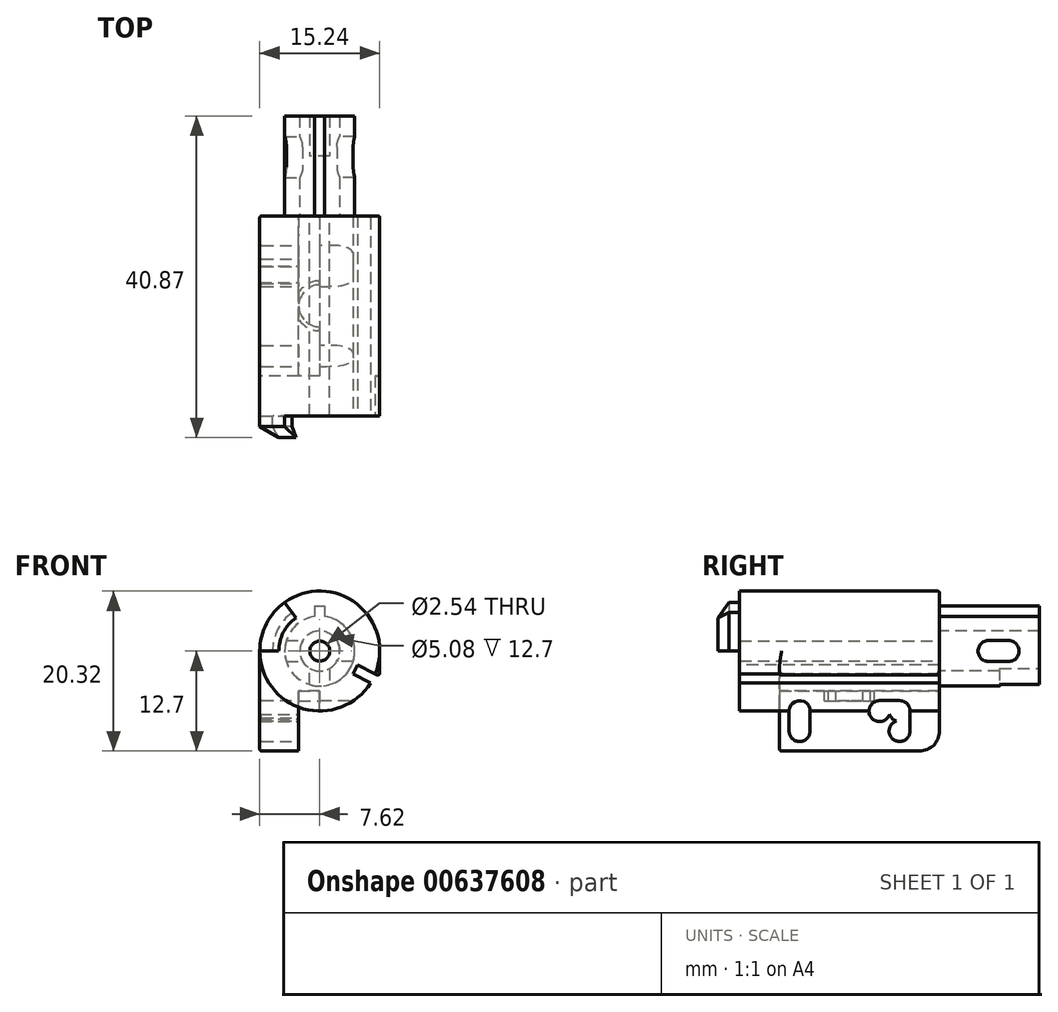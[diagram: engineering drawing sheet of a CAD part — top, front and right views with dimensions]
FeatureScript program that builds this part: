
annotation { "Feature Type Name" : "Feature", "Feature Type Description" : "" }
export const myFeature = defineFeature(function(context is Context, id is Id, definition is map)
    precondition{}
    {
        {
            var Q0;
            Q0=qCreatedBy(makeId("Front.planeOp"),FACE);
            var sketch = newSketch(context, id + "F0", { "sketchPlane" : qUnion([Q0])});
            skPoint(sketch, "E0.middle", {"position": v(0, 0) * mm});
            skLineSegment(sketch, "E1.bottom", {"start": v(7.62, 37.7) * mm, "end": v(-7.62, 37.7) * mm});
            skLineSegment(sketch, "E1.top", {"start": v(7.62, -37.7) * mm, "end": v(-7.62, -37.7) * mm});
            skLineSegment(sketch, "E1.left", {"start": v(7.62, 37.7) * mm, "end": v(7.62, -37.7) * mm});
            skLineSegment(sketch, "E1.right", {"start": v(-7.62, 37.7) * mm, "end": v(-7.62, -37.7) * mm});
            skCircle(sketch, "E2", {"center": v(0, 0) * mm, "radius": 7.62 * mm});
            skCircle(sketch, "E3", {"center": v(0, 0) * mm, "radius": 1.27 * mm});
            skSolve(sketch);
        }
        {
            var Q0;
            Q0=makeQuery(id+"F0.imprint","IMPRINT",FACE,{"disambiguationData":[TD([[makeQuery(id+"F0.imprint","IMPRINT",EDGE,{"derivedFrom":sQuery(id+"F0.wireOp",EDGE,"E3")}),-1.0]])]});
            extrude(context, id + "F1", {"entities" : qUnion([Q0]), "depth" : 12.7 * mm});
        }
        {
            var Q0;
            Q0=makeQuery(id+"F1.opExtrude","CAP_FACE",FACE,{"disambiguationData":[OSD([sQuery(id+"F0.wireOp",EDGE,"E2"),sQuery(id+"F0.wireOp",EDGE,"E3")])],"isStart":false});
            var sketch = newSketch(context, id + "F2", { "sketchPlane" : qUnion([Q0])});
            skArc(sketch, "E4", {"start": v(-7.62, 0) * mm, "mid": v(-6.78, 3.48) * mm, "end": v(-4.44, 6.2) * mm});
            skArc(sketch, "E5.0", {"start": v(-6, 0) * mm, "mid": v(-5.34, 2.74) * mm, "end": v(-3.5, 4.88) * mm});
            skLineSegment(sketch, "E6", {"start": v(-4.44, 6.2) * mm, "end": v(-3.5, 4.88) * mm});
            skLineSegment(sketch, "E7", {"start": v(-7.62, 0) * mm, "end": v(-6, 0) * mm});
            skSolve(sketch);
        }
        {
            var Q0;
            Q0=qSketchRegion(id+"F2",true);
            extrude(context, id + "F3", {"entities" : qUnion([Q0]), "operationType" : NewBodyOperationType.ADD, "depth" : 1.37 * mm});
        }
        {
            var Q0;
            Q0=makeQuery(id+"F3.opExtrude","CAP_FACE",FACE,{"disambiguationData":[OSD([sQuery(id+"F2.wireOp",EDGE,"E4"),sQuery(id+"F2.wireOp",EDGE,"E5.0"),sQuery(id+"F2.wireOp",EDGE,"E6"),sQuery(id+"F2.wireOp",EDGE,"E7")])],"isStart":false});
            cPlane(context, id + "F4", {"entities" : qUnion([Q0]), "cplaneType" : CPlaneType.OFFSET, "offset" : 1.4 * mm, "width" : 152.4 * mm, "height" : 152.4 * mm});
        }
        {
            var Q0;
            Q0=qCreatedBy(id+"F4.planeOp",FACE);
            var sketch = newSketch(context, id + "F5", { "sketchPlane" : qUnion([Q0])});
            skArc(sketch, "E8.0", {"start": v(-3.04, 4.23) * mm, "mid": v(-4.63, 2.38) * mm, "end": v(-5.2, 0) * mm});
            skSolve(sketch);
        }
        {
            var Q0;
            Q0=makeQuery(id+"F3.opExtrude","CAP_VERTEX",VERTEX,{"disambiguationData":[OSD([sQuery(id+"F0.wireOp",EDGE,"E2"),sQuery(id+"F2.wireOp",EDGE,"E4"),sQuery(id+"F2.wireOp",EDGE,"E7")])],"isStart":false});
            var Q1;
            Q1=makeQuery(id+"F3.opExtrude","CAP_VERTEX",VERTEX,{"disambiguationData":[OSD([sQuery(id+"F2.wireOp",EDGE,"E5.0"),sQuery(id+"F2.wireOp",EDGE,"E7")])],"isStart":false});
            var Q2;
            Q2=sQuery(id+"F5.wireOp",VERTEX,"E8.0.end");
            cPlane(context, id + "F6", {"entities" : qUnion([Q0, Q1, Q2]), "cplaneType" : CPlaneType.THREE_POINT, "offset" : 25.4 * mm, "width" : 152.4 * mm, "height" : 152.4 * mm});
        }
        {
            var Q0;
            Q0=qCreatedBy(id+"F6.planeOp",FACE);
            var sketch = newSketch(context, id + "F7", { "sketchPlane" : qUnion([Q0])});
            skPoint(sketch, "E9.0", {"position": v(-7.62, -14.07) * mm});
            skPoint(sketch, "E10.0", {"position": v(-6, -14.07) * mm});
            skPoint(sketch, "E11.0", {"position": v(-5.2, -15.47) * mm});
            skLineSegment(sketch, "E12", {"start": v(-7.62, -14.07) * mm, "end": v(-5.2, -15.47) * mm});
            skLineSegment(sketch, "E13", {"start": v(-5.2, -15.47) * mm, "end": v(-6, -14.07) * mm});
            skLineSegment(sketch, "E14", {"start": v(-6, -14.07) * mm, "end": v(-7.62, -14.07) * mm});
            skSolve(sketch);
        }
        {
            var Q0;
            Q0=makeQuery(id+"F3.opExtrude","CAP_VERTEX",VERTEX,{"disambiguationData":[OSD([sQuery(id+"F0.wireOp",EDGE,"E2"),sQuery(id+"F2.wireOp",EDGE,"E4"),sQuery(id+"F2.wireOp",EDGE,"E6")])],"isStart":false});
            var Q1;
            Q1=makeQuery(id+"F3.opExtrude","CAP_VERTEX",VERTEX,{"disambiguationData":[OSD([sQuery(id+"F2.wireOp",EDGE,"E5.0"),sQuery(id+"F2.wireOp",EDGE,"E6")])],"isStart":false});
            var Q2;
            Q2=sQuery(id+"F5.wireOp",VERTEX,"E8.0.start");
            cPlane(context, id + "F8", {"entities" : qUnion([Q0, Q1, Q2]), "cplaneType" : CPlaneType.THREE_POINT, "offset" : 25.4 * mm, "width" : 152.4 * mm, "height" : 152.4 * mm});
        }
        {
            var Q0;
            Q0=qCreatedBy(id+"F8.planeOp",FACE);
            var sketch = newSketch(context, id + "F9", { "sketchPlane" : qUnion([Q0])});
            skPoint(sketch, "E15.0", {"position": v(-14.07, 7.62) * mm});
            skPoint(sketch, "E16.0", {"position": v(-14.07, 6) * mm});
            skPoint(sketch, "E17.0", {"position": v(-15.47, 5.2) * mm});
            skLineSegment(sketch, "E18", {"start": v(-14.07, 7.62) * mm, "end": v(-14.07, 6) * mm});
            skLineSegment(sketch, "E19", {"start": v(-14.07, 6) * mm, "end": v(-15.47, 5.2) * mm});
            skLineSegment(sketch, "E20", {"start": v(-15.47, 5.2) * mm, "end": v(-14.07, 7.62) * mm});
            skSolve(sketch);
        }
        {
            var Q0;
            Q0=makeQuery(id+"F7.imprint","IMPRINT",FACE,{"disambiguationData":[TD([[makeQuery(id+"F7.imprint","IMPRINT",EDGE,{"derivedFrom":sQuery(id+"F7.wireOp",EDGE,"E12")}),1.0]])]});
            var Q1;
            Q1=makeQuery(id+"F9.imprint","IMPRINT",FACE,{"disambiguationData":[TD([[makeQuery(id+"F9.imprint","IMPRINT",EDGE,{"derivedFrom":sQuery(id+"F9.wireOp",EDGE,"E18")}),-1.0]])]});
            var Q2;
            Q2=makeQuery(id+"F7.imprint","IMPRINT",FACE,{"disambiguationData":[TD([[makeQuery(id+"F7.imprint","IMPRINT",EDGE,{"derivedFrom":sQuery(id+"F7.wireOp",EDGE,"E12")}),1.0]])]});
            var Q3;
            Q3=makeQuery(id+"F9.imprint","IMPRINT",FACE,{"disambiguationData":[TD([[makeQuery(id+"F9.imprint","IMPRINT",EDGE,{"derivedFrom":sQuery(id+"F9.wireOp",EDGE,"E18")}),-1.0]])]});
            var Q4;
            Q4=makeQuery(id+"F3.opExtrude","CAP_EDGE",EDGE,{"disambiguationData":[OSD([sQuery(id+"F2.wireOp",EDGE,"E4")])],"isStart":false});
            var Q5;
            Q5=makeQuery(id+"F3.opExtrude","CAP_EDGE",EDGE,{"disambiguationData":[OSD([sQuery(id+"F2.wireOp",EDGE,"E5.0")])],"isStart":false});
            var Q6;
            Q6=sQuery(id+"F5.wireOp",EDGE,"E8.0");
            loft(context, id + "F10", {"addGuides" : true, "sheetProfilesArray" : [{ "sheetProfileEntities" : qUnion([Q0]) }, { "sheetProfileEntities" : qUnion([Q1]) }], "wireProfilesArray" : [{ "wireProfileEntities" : qUnion([Q2]) }, { "wireProfileEntities" : qUnion([Q3]) }], "guidesArray" : [{ "guideEntities" : qUnion([Q4]), "guideDerivativeType" : LoftGuideDerivativeType.DEFAULT, "guideDerivativeMagnitude" : 1 }, { "guideEntities" : qUnion([Q5]), "guideDerivativeType" : LoftGuideDerivativeType.DEFAULT, "guideDerivativeMagnitude" : 1 }, { "guideEntities" : qUnion([Q6]), "guideDerivativeType" : LoftGuideDerivativeType.DEFAULT, "guideDerivativeMagnitude" : 1 }]});
        }
        {
            var Q0;
            Q0=makeQuery(id+"F1.opExtrude","CAP_FACE",FACE,{"disambiguationData":[OSD([sQuery(id+"F0.wireOp",EDGE,"E2"),sQuery(id+"F0.wireOp",EDGE,"E3")])],"isStart":true});
            var sketch = newSketch(context, id + "F11", { "sketchPlane" : qUnion([Q0])});
            skArc(sketch, "E21.0", {"start": v(-4.16, -6.39) * mm, "mid": v(-6.39, 4.16) * mm, "end": v(4.16, 6.39) * mm});
            skCircle(sketch, "E22", {"center": v(0, 0) * mm, "radius": 7.62 * mm});
            skSolve(sketch);
        }
        {
            var Q0;
            Q0=makeQuery(id+"F11.imprint","IMPRINT",FACE,{"disambiguationData":[TD([[makeQuery(id+"F11.imprint","IMPRINT",EDGE,{"derivedFrom":sQuery(id+"F11.wireOp",EDGE,"E22")}),1.0]])]});
            var Q1;
            Q1=makeQuery(id+"F11.imprint","IMPRINT",FACE,{"disambiguationData":[TD([[makeQuery(id+"F11.imprint","IMPRINT",EDGE,{"derivedFrom":makeQuery(id+"F1.opExtrude","CAP_EDGE",EDGE,{"disambiguationData":[OSD([sQuery(id+"F0.wireOp",EDGE,"E2")])],"isStart":true})}),-1.0]])]});
            var Q2;
            Q2=makeQuery(id+"F11.imprint","IMPRINT",FACE,{"disambiguationData":[TD([[makeQuery(id+"F11.imprint","IMPRINT",EDGE,{"derivedFrom":sQuery(id+"F11.wireOp",EDGE,"E22")}),-1.0]])]});
            extrude(context, id + "F12", {"entities" : qUnion([Q0, Q1, Q2]), "depth" : 12.7 * mm});
        }
        {
            var Q0;
            Q0=makeQuery(id+"FqKjOTA0KTiobea_0.opExtrude","SWEPT_BODY",BODY,{"disambiguationData":[OSD([sQuery(id+"F0.wireOp",EDGE,"uHF2WHmJ-zJ7i-FEed-3bSX-mTsy0IzEVw90"),sQuery(id+"F0.wireOp",EDGE,"k3DuiY5w-GI1o-rOdS-LLCr-VDr8IVeulzbr"),sQuery(id+"F0.wireOp",EDGE,"E1.left"),sQuery(id+"F0.wireOp",EDGE,"E1.right")])]});
            var Q1;
            Q1=makeQuery(id+"F1.opExtrude","SWEPT_BODY",BODY,{"disambiguationData":[OSD([sQuery(id+"F0.wireOp",EDGE,"E2"),sQuery(id+"F0.wireOp",EDGE,"E3")])]});
            var Q2;
            Q2=makeQuery(id+"F10.opLoft","SWEPT_BODY",BODY,{"disambiguationData":[OSD([sQuery(id+"F2.wireOp",EDGE,"E4"),sQuery(id+"F2.wireOp",EDGE,"E5.0"),sQuery(id+"F5.wireOp",EDGE,"E8.0"),makeQuery(id+"F7.imprint","IMPRINT",FACE,{"disambiguationData":[TD([[makeQuery(id+"F7.imprint","IMPRINT",EDGE,{"derivedFrom":sQuery(id+"F7.wireOp",EDGE,"E12")}),1.0]])]}),makeQuery(id+"F9.imprint","IMPRINT",FACE,{"disambiguationData":[TD([[makeQuery(id+"F9.imprint","IMPRINT",EDGE,{"derivedFrom":sQuery(id+"F9.wireOp",EDGE,"E18")}),-1.0]])]})])]});
            var Q3;
            Q3=makeQuery(id+"F12.opExtrude","SWEPT_BODY",BODY,{"disambiguationData":[OSD([sQuery(id+"F0.wireOp",EDGE,"E3"),sQuery(id+"F11.wireOp",EDGE,"E22")])]});
            booleanBodies(context, id + "F13", {"operationType" : BooleanOperationType.UNION, "tools" : qUnion([Q0, Q1, Q2, Q3])});
        }
        {
            var Q0;
            Q0=makeQuery(id+"F12.opExtrude","CAP_FACE",FACE,{"disambiguationData":[OSD([sQuery(id+"F0.wireOp",EDGE,"E3"),sQuery(id+"F11.wireOp",EDGE,"E22")])],"isStart":false});
            var sketch = newSketch(context, id + "F14", { "sketchPlane" : qUnion([Q0])});
            skCircle(sketch, "E23", {"center": v(0, 0) * mm, "radius": 7.62 * mm});
            skSolve(sketch);
        }
        {
            var Q0;
            Q0=makeQuery(id+"F14.imprint","IMPRINT",FACE,{"disambiguationData":[TD([[makeQuery(id+"F14.imprint","IMPRINT",EDGE,{"derivedFrom":sQuery(id+"F14.wireOp",EDGE,"E23")}),-1.0]])]});
            var sketch = newSketch(context, id + "F15", { "sketchPlane" : qUnion([Q0])});
            skCircle(sketch, "E24", {"center": v(0, 0) * mm, "radius": 4.45 * mm});
            skCircle(sketch, "E25", {"center": v(0, 0) * mm, "radius": 2.54 * mm});
            skSolve(sketch);
        }
        {
            var Q0;
            Q0=makeQuery(id+"F15.imprint","IMPRINT",FACE,{"disambiguationData":[TD([[makeQuery(id+"F15.imprint","IMPRINT",EDGE,{"derivedFrom":sQuery(id+"F15.wireOp",EDGE,"E24")}),1.0]])]});
            var Q1;
            Q1=qSketchRegion(id+"F17",true);
            extrude(context, id + "F16", {"entities" : qUnion([Q0, Q1]), "operationType" : NewBodyOperationType.ADD, "depth" : 12.7 * mm});
        }
        {
            var Q0;
            Q0=qCreatedBy(makeId("Right.planeOp"),FACE);
            var sketch = newSketch(context, id + "F17", { "sketchPlane" : qUnion([Q0])});
            skArc(sketch, "E26", {"start": v(18.92, 1.33) * mm, "mid": v(17.59, 0) * mm, "end": v(18.92, -1.33) * mm});
            skArc(sketch, "E27", {"start": v(21.46, -1.33) * mm, "mid": v(22.8, 0) * mm, "end": v(21.46, 1.33) * mm});
            skLineSegment(sketch, "E28", {"start": v(21.46, 0) * mm, "end": v(21.46, 1.33) * mm});
            skLineSegment(sketch, "E29", {"start": v(21.46, 1.33) * mm, "end": v(18.92, 1.33) * mm});
            skLineSegment(sketch, "E30", {"start": v(18.92, 1.33) * mm, "end": v(18.92, 0) * mm});
            skLineSegment(sketch, "E31", {"start": v(21.46, 0) * mm, "end": v(21.46, -1.33) * mm});
            skLineSegment(sketch, "E32", {"start": v(21.46, -1.33) * mm, "end": v(18.92, -1.33) * mm});
            skLineSegment(sketch, "E33", {"start": v(18.92, -1.33) * mm, "end": v(18.92, 0) * mm});
            skSolve(sketch);
        }
        {
            var Q0;
            Q0=qSketchRegion(id+"F17",true);
            extrude(context, id + "F18", {"entities" : qUnion([Q0]), "operationType" : NewBodyOperationType.REMOVE, "oppositeDirection" : true, "depth" : 25.4 * mm});
        }
        {
            var Q0;
            Q0=qSketchRegion(id+"F17",true);
            var Q1;
            {var subQ0=sQuery(id+"F17.wireOp",EDGE,"E27");var subQ1=sQuery(id+"F17.wireOp",EDGE,"E26");var subQ2=makeQuery(id+"F17.imprint","INTERSECT",VERTEX,{"disambiguationData":[OD(0.0)],"derivedFrom":[subQ1,subQ0]});Q1=makeQuery(id+"F17.imprint","IMPRINT",FACE,{"disambiguationData":[TD([[makeQuery(id+"F17.imprint","IMPRINT",EDGE,{"disambiguationData":[TD([[subQ2,1.0]])],"derivedFrom":subQ1}),1.0]])]});}
            extrude(context, id + "F19", {"entities" : qUnion([Q0, Q1]), "operationType" : NewBodyOperationType.REMOVE, "depth" : 25.4 * mm});
        }
        {
            var Q0;
            Q0=makeQuery(id+"F16.opExtrude","CAP_FACE",FACE,{"disambiguationData":[OSD([sQuery(id+"F15.wireOp",EDGE,"E24"),sQuery(id+"F15.wireOp",EDGE,"E25")])],"isStart":false});
            var sketch = newSketch(context, id + "F20", { "sketchPlane" : qUnion([Q0])});
            skLineSegment(sketch, "E34", {"start": v(0, -2.54) * mm, "end": v(0, -4.45) * mm});
            skLineSegment(sketch, "E35", {"start": v(0, -4.45) * mm, "end": v(-1.27, -4.45) * mm});
            skLineSegment(sketch, "E36", {"start": v(-1.27, -4.45) * mm, "end": v(1.27, -4.45) * mm});
            skLineSegment(sketch, "E37", {"start": v(1.27, -4.45) * mm, "end": v(1.27, -2.2) * mm});
            skLineSegment(sketch, "E38", {"start": v(1.27, -2.2) * mm, "end": v(-1.27, -2.2) * mm});
            skLineSegment(sketch, "E39", {"start": v(-1.27, -2.2) * mm, "end": v(-1.27, -4.45) * mm});
            skSolve(sketch);
        }
        {
            var Q0;
            {var subQ0=sQuery(id+"F20.wireOp",EDGE,"E36");var subQ3=sQuery(id+"F20.wireOp",EDGE,"E39");var subQ4=makeQuery(id+"F20.imprint","INTERSECT",VERTEX,{"derivedFrom":[subQ0,subQ3]});Q0=makeQuery(id+"F20.imprint","IMPRINT",FACE,{"disambiguationData":[TD([[makeQuery(id+"F20.imprint","IMPRINT",EDGE,{"disambiguationData":[TD([[subQ4,1.0]])],"derivedFrom":subQ3}),1.0]])]});}
            var Q1;
            {var subQ0=sQuery(id+"F20.wireOp",EDGE,"E36");var subQ3=sQuery(id+"F20.wireOp",EDGE,"E37");var subQ4=makeQuery(id+"F20.imprint","INTERSECT",VERTEX,{"derivedFrom":[subQ0,subQ3]});Q1=makeQuery(id+"F20.imprint","IMPRINT",FACE,{"disambiguationData":[TD([[makeQuery(id+"F20.imprint","IMPRINT",EDGE,{"disambiguationData":[TD([[subQ4,-1.0]])],"derivedFrom":subQ3}),1.0]])]});}
            var Q2;
            {var subQ0=sQuery(id+"F20.wireOp",EDGE,"E38");Q2=makeQuery(id+"F20.imprint","IMPRINT",FACE,{"disambiguationData":[TD([[makeQuery(id+"F20.imprint","IMPRINT",EDGE,{"derivedFrom":subQ0}),1.0]])]});}
            var Q3;
            {var subQ0=sQuery(id+"F20.wireOp",EDGE,"E34");Q3=makeQuery(id+"F20.imprint","IMPRINT",FACE,{"disambiguationData":[TD([[makeQuery(id+"F20.imprint","IMPRINT",EDGE,{"derivedFrom":subQ0}),1.0]])]});}
            var Q4;
            {var subQ0=sQuery(id+"F20.wireOp",EDGE,"E34");Q4=makeQuery(id+"F20.imprint","IMPRINT",FACE,{"disambiguationData":[TD([[makeQuery(id+"F20.imprint","IMPRINT",EDGE,{"derivedFrom":subQ0}),-1.0]])]});}
            extrude(context, id + "F21", {"entities" : qUnion([Q0, Q1, Q2, Q3, Q4]), "operationType" : NewBodyOperationType.REMOVE, "oppositeDirection" : true, "depth" : 5.08 * mm});
        }
        {
            var Q0;
            Q0=makeQuery(id+"F16.opExtrude","CAP_FACE",FACE,{"disambiguationData":[OSD([sQuery(id+"F15.wireOp",EDGE,"E24"),sQuery(id+"F15.wireOp",EDGE,"E25")])],"isStart":false});
            var sketch = newSketch(context, id + "F22", { "sketchPlane" : qUnion([Q0])});
            skLineSegment(sketch, "E40", {"start": v(0, 4.45) * mm, "end": v(0, 5.72) * mm});
            skPoint(sketch, "E40.endSnap0", {"position": v(0, 4.45) * mm});
            skLineSegment(sketch, "E41", {"start": v(0, 5.72) * mm, "end": v(0.64, 5.72) * mm});
            skLineSegment(sketch, "E42", {"start": v(0.64, 5.72) * mm, "end": v(-0.64, 5.72) * mm});
            skLineSegment(sketch, "E43", {"start": v(-0.64, 5.72) * mm, "end": v(-0.64, 4.4) * mm});
            skLineSegment(sketch, "E44", {"start": v(0.64, 5.72) * mm, "end": v(0.64, 4.4) * mm});
            skSolve(sketch);
        }
        {
            var Q0;
            {var subQ0=sQuery(id+"F22.wireOp",EDGE,"E40");Q0=makeQuery(id+"F22.imprint","IMPRINT",FACE,{"disambiguationData":[TD([[makeQuery(id+"F22.imprint","IMPRINT",EDGE,{"derivedFrom":subQ0}),1.0]])]});}
            var Q1;
            {var subQ0=sQuery(id+"F22.wireOp",EDGE,"E40");Q1=makeQuery(id+"F22.imprint","IMPRINT",FACE,{"disambiguationData":[TD([[makeQuery(id+"F22.imprint","IMPRINT",EDGE,{"derivedFrom":subQ0}),1.0]])]});}
            var Q2;
            {var subQ0=sQuery(id+"F22.wireOp",EDGE,"E40");Q2=makeQuery(id+"F22.imprint","IMPRINT",FACE,{"disambiguationData":[TD([[makeQuery(id+"F22.imprint","IMPRINT",EDGE,{"derivedFrom":subQ0}),-1.0]])]});}
            extrude(context, id + "F23", {"entities" : qUnion([Q0, Q1, Q2]), "operationType" : NewBodyOperationType.ADD, "oppositeDirection" : true, "depth" : 12.7 * mm});
        }
        {
            var Q0;
            Q0=makeQuery(id+"F1.opExtrude","CAP_FACE",FACE,{"disambiguationData":[OSD([sQuery(id+"F0.wireOp",EDGE,"E2"),sQuery(id+"F0.wireOp",EDGE,"E3")])],"isStart":false});
            var sketch = newSketch(context, id + "F24", { "sketchPlane" : qUnion([Q0])});
            skLineSegment(sketch, "E45", {"start": v(-5.34, 2.74) * mm, "end": v(0, 0) * mm});
            skLineSegment(sketch, "E46", {"start": v(4.52, -2.32) * mm, "end": v(4.8, -1.75) * mm});
            skLineSegment(sketch, "E47", {"start": v(4.8, -1.75) * mm, "end": v(4.23, -2.88) * mm});
            skLineSegment(sketch, "E48", {"start": v(4.8, -1.75) * mm, "end": v(7.05, -2.9) * mm});
            skLineSegment(sketch, "E49", {"start": v(4.23, -2.88) * mm, "end": v(6.47, -4.03) * mm});
            skLineSegment(sketch, "E50", {"start": v(0, 0) * mm, "end": v(4.52, -2.32) * mm});
            skLineSegment(sketch, "E51", {"start": v(4.52, -2.32) * mm, "end": v(6.78, -3.48) * mm});
            skSolve(sketch);
        }
        {
            var Q0;
            {var subQ0=sQuery(id+"F24.wireOp",EDGE,"E48");Q0=makeQuery(id+"F24.imprint","IMPRINT",FACE,{"disambiguationData":[TD([[makeQuery(id+"F24.imprint","IMPRINT",EDGE,{"derivedFrom":subQ0}),-1.0]])]});}
            var Q1;
            {var subQ0=sQuery(id+"F24.wireOp",EDGE,"E49");Q1=makeQuery(id+"F24.imprint","IMPRINT",FACE,{"disambiguationData":[TD([[makeQuery(id+"F24.imprint","IMPRINT",EDGE,{"derivedFrom":subQ0}),1.0]])]});}
            extrude(context, id + "F25", {"entities" : qUnion([Q0, Q1]), "operationType" : NewBodyOperationType.REMOVE, "oppositeDirection" : true, "depth" : 25.4 * mm});
        }
        {
            var Q0;
            Q0=makeQuery(id+"F14.imprint","IMPRINT",FACE,{"disambiguationData":[TD([[makeQuery(id+"F14.imprint","IMPRINT",EDGE,{"derivedFrom":sQuery(id+"F14.wireOp",EDGE,"E23")}),-1.0]])]});
            cPlane(context, id + "F26", {"entities" : qUnion([Q0]), "cplaneType" : CPlaneType.OFFSET, "offset" : 20.32 * mm, "oppositeDirection" : true, "width" : 152.4 * mm, "height" : 152.4 * mm});
        }
        {
            var Q0;
            Q0=qCreatedBy(id+"F26.planeOp",FACE);
            var sketch = newSketch(context, id + "F27", { "sketchPlane" : qUnion([Q0])});
            skLineSegment(sketch, "E52.0.0", {"start": v(-6.47, -4.03) * mm, "end": v(-4.23, -2.88) * mm});
            skLineSegment(sketch, "E52.0.1", {"start": v(-4.23, -2.88) * mm, "end": v(-4.8, -1.75) * mm});
            skLineSegment(sketch, "E52.0.2", {"start": v(-4.8, -1.75) * mm, "end": v(-7.05, -2.9) * mm});
            skArc(sketch, "E52.0.3", {"start": v(-7.05, -2.9) * mm, "mid": v(-4.73, 5.97) * mm, "end": v(4.44, 6.2) * mm});
            skLineSegment(sketch, "E52.0.4", {"start": v(4.44, 6.2) * mm, "end": v(3.5, 4.88) * mm});
            skArc(sketch, "E52.0.5", {"start": v(3.5, 4.88) * mm, "mid": v(5.34, 2.74) * mm, "end": v(6, 0) * mm});
            skLineSegment(sketch, "E52.0.6", {"start": v(6, 0) * mm, "end": v(7.62, 0) * mm});
            skArc(sketch, "E52.0.7", {"start": v(7.62, 0) * mm, "mid": v(2.1, -7.33) * mm, "end": v(-6.47, -4.03) * mm});
            skLineSegment(sketch, "E53", {"start": v(0, 0) * mm, "end": v(-7.62, 0) * mm});
            skLineSegment(sketch, "E54", {"start": v(-7.62, 0) * mm, "end": v(7.62, 0) * mm});
            skLineSegment(sketch, "E55", {"start": v(7.62, 0) * mm, "end": v(7.62, -12.7) * mm});
            skLineSegment(sketch, "E56", {"start": v(-7.62, 0) * mm, "end": v(-7.62, -12.7) * mm});
            skLineSegment(sketch, "E57", {"start": v(-7.62, -12.7) * mm, "end": v(7.62, -12.7) * mm});
            skLineSegment(sketch, "E58", {"start": v(0, 0) * mm, "end": v(0, -12.7) * mm});
            skLineSegment(sketch, "E59", {"start": v(-4.8, -1.75) * mm, "end": v(-7.62, -3.2) * mm});
            skLineSegment(sketch, "E60", {"start": v(-4.8, -1.75) * mm, "end": v(-4.23, -2.88) * mm});
            skLineSegment(sketch, "E61", {"start": v(-4.23, -2.88) * mm, "end": v(-7.62, -4.62) * mm});
            skPoint(sketch, "E61.endSnap0", {"position": v(-7.62, -6.35) * mm});
            skSolve(sketch);
        }
        {
            var Q0;
            {var subQ3=sQuery(id+"F27.wireOp",EDGE,"E52.0.7");var subQ5=sQuery(id+"F27.wireOp",EDGE,"E61");var subQ6=makeQuery(id+"F27.imprint","INTERSECT",VERTEX,{"derivedFrom":[subQ3,subQ5]});Q0=makeQuery(id+"F27.imprint","IMPRINT",FACE,{"disambiguationData":[TD([[makeQuery(id+"F27.imprint","IMPRINT",EDGE,{"disambiguationData":[TD([[subQ6,1.0]])],"derivedFrom":subQ3}),1.0]])]});}
            var Q1;
            {var subQ0=sQuery(id+"F27.wireOp",EDGE,"E55");Q1=makeQuery(id+"F27.imprint","IMPRINT",FACE,{"disambiguationData":[TD([[makeQuery(id+"F27.imprint","IMPRINT",EDGE,{"derivedFrom":subQ0}),-1.0]])]});}
            var Q2;
            {var subQ0=sQuery(id+"F27.wireOp",EDGE,"E59");var subQ1=sQuery(id+"F27.wireOp",EDGE,"E52.0.3");var subQ2=makeQuery(id+"F27.imprint","INTERSECT",VERTEX,{"derivedFrom":[subQ1,subQ0]});Q2=makeQuery(id+"F27.imprint","IMPRINT",FACE,{"disambiguationData":[TD([[makeQuery(id+"F27.imprint","IMPRINT",EDGE,{"disambiguationData":[TD([[subQ2,-1.0]])],"derivedFrom":subQ0}),-1.0]])]});}
            extrude(context, id + "F28", {"entities" : qUnion([Q0, Q1, Q2]), "operationType" : NewBodyOperationType.ADD, "depth" : 20.32 * mm});
        }
        {
            var Q0;
            Q0=makeQuery(id+"F28.opExtrude","SWEPT_FACE",FACE,{"disambiguationData":[OSD([sQuery(id+"F27.wireOp",EDGE,"E57")])]});
            var sketch = newSketch(context, id + "F29", { "sketchPlane" : qUnion([Q0])});
            skLineSegment(sketch, "E62", {"start": v(-2.67, 7.62) * mm, "end": v(-2.67, -12.7) * mm});
            skLineSegment(sketch, "E63", {"start": v(2.67, 7.62) * mm, "end": v(2.67, -12.7) * mm});
            skSolve(sketch);
        }
        {
            var Q0;
            Q0=qSketchRegion(id+"F29",true);
            var Q1;
            {var subQ0=sQuery(id+"F29.wireOp",EDGE,"E62");Q1=makeQuery(id+"F29.imprint","IMPRINT",FACE,{"disambiguationData":[TD([[makeQuery(id+"F29.imprint","IMPRINT",EDGE,{"derivedFrom":subQ0}),1.0]])]});}
            extrude(context, id + "F30", {"entities" : qUnion([Q0, Q1]), "operationType" : NewBodyOperationType.REMOVE, "oppositeDirection" : true, "depth" : 7.62 * mm});
        }
        {
            var Q0;
            {var subQ0=sQuery(id+"F27.wireOp",EDGE,"E56");Q0=makeQuery(id+"F28.opExtrude","SWEPT_FACE",FACE,{"disambiguationData":[OSD([subQ0]),TDD([makeQuery(id+"F27.imprint","IMPRINT",EDGE,{"disambiguationData":[TD([[makeQuery(id+"F27.imprint","INTERSECT",VERTEX,{"derivedFrom":[subQ0,sQuery(id+"F27.wireOp",EDGE,"E57")]}),1.0]])],"derivedFrom":subQ0})])]});}
            var sketch = newSketch(context, id + "F31", { "sketchPlane" : qUnion([Q0])});
            skCircle(sketch, "E64", {"center": v(-5.08, -10.16) * mm, "radius": 1.33 * mm});
            skCircle(sketch, "E65", {"center": v(7.62, -10.16) * mm, "radius": 1.33 * mm});
            skCircle(sketch, "E66", {"center": v(7.62, -7.62) * mm, "radius": 1.33 * mm});
            skCircle(sketch, "E67", {"center": v(-5.08, -7.62) * mm, "radius": 1.33 * mm});
            skCircle(sketch, "E68", {"center": v(5.08, -7.62) * mm, "radius": 1.33 * mm});
            skLineSegment(sketch, "E69", {"start": v(4.08, -8.5) * mm, "end": v(6.68, -11.1) * mm});
            skLineSegment(sketch, "E70", {"start": v(6.68, -11.1) * mm, "end": v(4.08, -8.5) * mm});
            skLineSegment(sketch, "E71", {"start": v(7.62, -7.62) * mm, "end": v(8.95, -7.62) * mm});
            skLineSegment(sketch, "E72", {"start": v(8.95, -7.62) * mm, "end": v(8.95, -10.16) * mm});
            skLineSegment(sketch, "E73", {"start": v(7.62, -7.62) * mm, "end": v(7.62, -6.29) * mm});
            skLineSegment(sketch, "E74", {"start": v(7.62, -6.29) * mm, "end": v(5.08, -6.29) * mm});
            skLineSegment(sketch, "E75", {"start": v(-5.08, -7.62) * mm, "end": v(-3.75, -7.62) * mm});
            skLineSegment(sketch, "E76", {"start": v(-3.75, -7.62) * mm, "end": v(-3.75, -10.16) * mm});
            skLineSegment(sketch, "E77", {"start": v(-3.75, -10.16) * mm, "end": v(-6.41, -10.16) * mm});
            skLineSegment(sketch, "E78", {"start": v(-6.41, -10.16) * mm, "end": v(-6.41, -7.62) * mm});
            skSolve(sketch);
        }
        {
            var Q0;
            {var subQ0=sQuery(id+"F31.wireOp",EDGE,"E67");var subQ1=makeQuery(id+"F31.imprint","INTERSECT",VERTEX,{"derivedFrom":[subQ0,sQuery(id+"F31.wireOp",EDGE,"E76")]});Q0=makeQuery(id+"F31.imprint","IMPRINT",FACE,{"disambiguationData":[TD([[makeQuery(id+"F31.imprint","IMPRINT",EDGE,{"disambiguationData":[TD([[subQ1,-1.0]])],"derivedFrom":subQ0}),1.0]])]});}
            var Q1;
            {var subQ0=sQuery(id+"F31.wireOp",EDGE,"E77");Q1=makeQuery(id+"F31.imprint","IMPRINT",FACE,{"disambiguationData":[TD([[makeQuery(id+"F31.imprint","IMPRINT",EDGE,{"derivedFrom":subQ0}),1.0]])]});}
            var Q2;
            {var subQ0=sQuery(id+"F31.wireOp",EDGE,"E76");Q2=makeQuery(id+"F31.imprint","IMPRINT",FACE,{"disambiguationData":[TD([[makeQuery(id+"F31.imprint","IMPRINT",EDGE,{"derivedFrom":subQ0}),-1.0]])]});}
            var Q3;
            {var subQ0=sQuery(id+"F31.wireOp",EDGE,"E78");Q3=makeQuery(id+"F31.imprint","IMPRINT",FACE,{"disambiguationData":[TD([[makeQuery(id+"F31.imprint","IMPRINT",EDGE,{"derivedFrom":subQ0}),-1.0]])]});}
            var Q4;
            {var subQ0=sQuery(id+"F31.wireOp",EDGE,"E70");var subQ1=sQuery(id+"F31.wireOp",EDGE,"E65");var subQ2=makeQuery(id+"F31.imprint","INTERSECT",VERTEX,{"derivedFrom":[subQ1,subQ0]});Q4=makeQuery(id+"F31.imprint","IMPRINT",FACE,{"disambiguationData":[TD([[makeQuery(id+"F31.imprint","IMPRINT",EDGE,{"disambiguationData":[TD([[subQ2,1.0]])],"derivedFrom":subQ1}),-1.0]])]});}
            var Q5;
            {var subQ0=sQuery(id+"F31.wireOp",EDGE,"E74");Q5=makeQuery(id+"F31.imprint","IMPRINT",FACE,{"disambiguationData":[TD([[makeQuery(id+"F31.imprint","IMPRINT",EDGE,{"derivedFrom":subQ0}),1.0]])]});}
            var Q6;
            {var subQ0=sQuery(id+"F31.wireOp",EDGE,"E71");Q6=makeQuery(id+"F31.imprint","IMPRINT",FACE,{"disambiguationData":[TD([[makeQuery(id+"F31.imprint","IMPRINT",EDGE,{"derivedFrom":subQ0}),-1.0]])]});}
            var Q7;
            {var subQ0=sQuery(id+"F31.wireOp",EDGE,"E71");Q7=makeQuery(id+"F31.imprint","IMPRINT",FACE,{"disambiguationData":[TD([[makeQuery(id+"F31.imprint","IMPRINT",EDGE,{"derivedFrom":subQ0}),1.0]])]});}
            var Q8;
            {var subQ0=sQuery(id+"F31.wireOp",EDGE,"E65");var subQ1=makeQuery(id+"F31.imprint","INTERSECT",VERTEX,{"derivedFrom":[subQ0,sQuery(id+"F31.wireOp",EDGE,"E72")]});Q8=makeQuery(id+"F31.imprint","IMPRINT",FACE,{"disambiguationData":[TD([[makeQuery(id+"F31.imprint","IMPRINT",EDGE,{"disambiguationData":[TD([[subQ1,-1.0]])],"derivedFrom":subQ0}),1.0]])]});}
            var Q9;
            {var subQ0=sQuery(id+"F31.wireOp",EDGE,"E72");Q9=makeQuery(id+"F31.imprint","IMPRINT",FACE,{"disambiguationData":[TD([[makeQuery(id+"F31.imprint","IMPRINT",EDGE,{"derivedFrom":subQ0}),-1.0]])]});}
            var Q10;
            {var subQ0=sQuery(id+"F31.wireOp",EDGE,"E68");var subQ1=sQuery(id+"F31.wireOp",EDGE,"E66");var subQ2=makeQuery(id+"F31.imprint","INTERSECT",VERTEX,{"disambiguationData":[OD(0.0)],"derivedFrom":[subQ1,subQ0]});Q10=makeQuery(id+"F31.imprint","IMPRINT",FACE,{"disambiguationData":[TD([[makeQuery(id+"F31.imprint","IMPRINT",EDGE,{"disambiguationData":[TD([[subQ2,-1.0]])],"derivedFrom":subQ1}),1.0]])]});}
            var Q11;
            {var subQ0=sQuery(id+"F31.wireOp",EDGE,"E66");var subQ1=sQuery(id+"F31.wireOp",EDGE,"E65");var subQ2=makeQuery(id+"F31.imprint","INTERSECT",VERTEX,{"disambiguationData":[OD(0.0)],"derivedFrom":[subQ1,subQ0]});Q11=makeQuery(id+"F31.imprint","IMPRINT",FACE,{"disambiguationData":[TD([[makeQuery(id+"F31.imprint","IMPRINT",EDGE,{"disambiguationData":[TD([[subQ2,-1.0]])],"derivedFrom":subQ1}),1.0]])]});}
            var Q12;
            {var subQ0=sQuery(id+"F31.wireOp",EDGE,"E68");var subQ1=sQuery(id+"F31.wireOp",EDGE,"E66");var subQ5=makeQuery(id+"F31.imprint","INTERSECT",VERTEX,{"disambiguationData":[OD(0.0)],"derivedFrom":[subQ1,subQ0]});Q12=makeQuery(id+"F31.imprint","IMPRINT",FACE,{"disambiguationData":[TD([[makeQuery(id+"F31.imprint","IMPRINT",EDGE,{"disambiguationData":[TD([[subQ5,-1.0]])],"derivedFrom":subQ1}),-1.0]])]});}
            var Q13;
            {var subQ0=sQuery(id+"F31.wireOp",EDGE,"E77");Q13=makeQuery(id+"F31.imprint","IMPRINT",FACE,{"disambiguationData":[TD([[makeQuery(id+"F31.imprint","IMPRINT",EDGE,{"derivedFrom":subQ0}),-1.0]])]});}
            var Q14;
            {var subQ0=sQuery(id+"F31.wireOp",EDGE,"E67");var subQ1=sQuery(id+"F31.wireOp",EDGE,"E64");var subQ2=makeQuery(id+"F31.imprint","INTERSECT",VERTEX,{"disambiguationData":[OD(0.0)],"derivedFrom":[subQ1,subQ0]});Q14=makeQuery(id+"F31.imprint","IMPRINT",FACE,{"disambiguationData":[TD([[makeQuery(id+"F31.imprint","IMPRINT",EDGE,{"disambiguationData":[TD([[subQ2,-1.0]])],"derivedFrom":subQ1}),1.0]])]});}
            extrude(context, id + "F32", {"entities" : qUnion([Q0, Q1, Q2, Q3, Q4, Q5, Q6, Q7, Q8, Q9, Q10, Q11, Q12, Q13, Q14]), "operationType" : NewBodyOperationType.REMOVE, "oppositeDirection" : true, "depth" : 25.4 * mm});
        }
        {
            var Q0;
            Q0=makeQuery(id+"F30.boolean.opBoolean","COPY",FACE,{"derivedFrom":makeQuery(id+"F30.opExtrude","CAP_FACE",FACE,{"disambiguationData":[OSD([sQuery(id+"F27.wireOp",EDGE,"E57"),sQuery(id+"F29.wireOp",EDGE,"E62"),sQuery(id+"F29.wireOp",EDGE,"E63")])],"isStart":false})});
            var sketch = newSketch(context, id + "F33", { "sketchPlane" : qUnion([Q0])});
            skLineSegment(sketch, "E79", {"start": v(0, 7.62) * mm, "end": v(0, -1.27) * mm});
            skLineSegment(sketch, "E80", {"start": v(0, -1.27) * mm, "end": v(0, -12.7) * mm});
            skCircle(sketch, "E81", {"center": v(0, -1.27) * mm, "radius": 2.67 * mm});
            skCircle(sketch, "E82", {"center": v(0, -1.27) * mm, "radius": 3.18 * mm});
            skSolve(sketch);
        }
        {
            var Q0;
            Q0=qSketchRegion(id+"F33",true);
            extrude(context, id + "F34", {"entities" : qUnion([Q0]), "operationType" : NewBodyOperationType.ADD, "depth" : 1.27 * mm});
        }
        {
            var Q0;
            Q0=makeQuery(id+"F12.opExtrude","CAP_EDGE",EDGE,{"disambiguationData":[OSD([sQuery(id+"F11.wireOp",EDGE,"E22")])],"isStart":false});
            var Q1;
            {var subQ0=sQuery(id+"F27.wireOp",EDGE,"E56");Q1=makeQuery(id+"F28.opExtrude","CAP_EDGE",EDGE,{"disambiguationData":[OSD([subQ0]),TDD([makeQuery(id+"F27.imprint","IMPRINT",EDGE,{"disambiguationData":[TD([[makeQuery(id+"F27.imprint","INTERSECT",VERTEX,{"derivedFrom":[subQ0,sQuery(id+"F27.wireOp",EDGE,"E57")]}),1.0]])],"derivedFrom":subQ0})])],"isStart":true});}
            var Q2;
            Q2=makeQuery(id+"F28.opExtrude","SWEPT_EDGE",EDGE,{"disambiguationData":[OSD([sQuery(id+"F27.wireOp",EDGE,"E56"),sQuery(id+"F27.wireOp",EDGE,"E57")])]});
            var Q3;
            {var subQ0=sQuery(id+"F27.wireOp",EDGE,"E56");Q3=makeQuery(id+"F28.opExtrude","CAP_EDGE",EDGE,{"disambiguationData":[OSD([subQ0]),TDD([makeQuery(id+"F27.imprint","IMPRINT",EDGE,{"disambiguationData":[TD([[makeQuery(id+"F27.imprint","INTERSECT",VERTEX,{"derivedFrom":[subQ0,sQuery(id+"F27.wireOp",EDGE,"E57")]}),1.0]])],"derivedFrom":subQ0})])],"isStart":false});}
            var Q4;
            Q4=makeQuery(id+"F28.opExtrude","CAP_EDGE",EDGE,{"disambiguationData":[OSD([sQuery(id+"F27.wireOp",EDGE,"E55")])],"isStart":false});
            var Q5;
            Q5=makeQuery(id+"F28.opExtrude","SWEPT_EDGE",EDGE,{"disambiguationData":[OSD([sQuery(id+"F27.wireOp",EDGE,"E55"),sQuery(id+"F27.wireOp",EDGE,"E57")])]});
            var Q6;
            {var subQ1=sQuery(id+"F27.wireOp",EDGE,"E57");Q6=makeQuery(id+"F30.boolean.opBoolean","SPLIT",EDGE,{"disambiguationData":[TD([makeQuery(id+"F30.opExtrude","SWEPT_FACE",FACE,{"disambiguationData":[OSD([sQuery(id+"F29.wireOp",EDGE,"E63")])]})])],"derivedFrom":makeQuery(id+"F28.opExtrude","CAP_EDGE",EDGE,{"disambiguationData":[OSD([subQ1])],"isStart":true})});}
            var Q7;
            {var subQ0=sQuery(id+"F27.wireOp",EDGE,"E57");var subQ1=sQuery(id+"F27.wireOp",EDGE,"E55");Q7=makeQuery(id+"F30.boolean.opBoolean","SPLIT",EDGE,{"disambiguationData":[TD([makeQuery(id+"F28.opExtrude","SWEPT_FACE",FACE,{"disambiguationData":[OSD([subQ1])]})])],"derivedFrom":makeQuery(id+"F28.opExtrude","CAP_EDGE",EDGE,{"disambiguationData":[OSD([subQ0])],"isStart":true})});}
            var Q8;
            Q8=makeQuery(id+"F28.opExtrude","CAP_EDGE",EDGE,{"disambiguationData":[OSD([sQuery(id+"F27.wireOp",EDGE,"E55")])],"isStart":true});
            var Q9;
            Q9=makeQuery(id+"F25.boolean.opBoolean","COPY",EDGE,{"derivedFrom":makeQuery(id+"F25.opExtrude","CAP_EDGE",EDGE,{"disambiguationData":[OSD([sQuery(id+"F24.wireOp",EDGE,"E48")])],"isStart":false})});
            var Q10;
            Q10=makeQuery(id+"F25.boolean.opBoolean","COPY",EDGE,{"derivedFrom":makeQuery(id+"F25.opExtrude","CAP_EDGE",EDGE,{"disambiguationData":[OSD([sQuery(id+"F24.wireOp",EDGE,"E49")])],"isStart":false})});
            fillet(context, id + "F35", {"entities" : qUnion([Q0, Q1, Q2, Q3, Q4, Q5, Q6, Q7, Q8, Q9, Q10]), "radius" : 0.25 * mm, "tangentPropagation" : true, "allowEdgeOverflow" : false});
        }
        {
            var Q0;
            Q0=makeQuery(id+"F32.boolean.opBoolean","COPY",EDGE,{"derivedFrom":makeQuery(id+"F32.opExtrude","CAP_EDGE",EDGE,{"disambiguationData":[OSD([sQuery(id+"F31.wireOp",EDGE,"E74")])],"isStart":true})});
            var Q1;
            Q1=makeQuery(id+"F32.boolean.opBoolean","COPY",EDGE,{"derivedFrom":makeQuery(id+"F32.opExtrude","CAP_EDGE",EDGE,{"disambiguationData":[OSD([sQuery(id+"F31.wireOp",EDGE,"E76")])],"isStart":true})});
            var Q2;
            Q2=makeQuery(id+"F32.boolean.opBoolean","INTERSECT",EDGE,{"derivedFrom":[makeQuery(id+"F28.opExtrude","SWEPT_FACE",FACE,{"disambiguationData":[OSD([sQuery(id+"F27.wireOp",EDGE,"E55")])]}),makeQuery(id+"F32.opExtrude","SWEPT_FACE",FACE,{"disambiguationData":[OSD([sQuery(id+"F31.wireOp",EDGE,"E76")])]})]});
            var Q3;
            Q3=makeQuery(id+"F32.boolean.opBoolean","INTERSECT",EDGE,{"derivedFrom":[makeQuery(id+"F28.opExtrude","SWEPT_FACE",FACE,{"disambiguationData":[OSD([sQuery(id+"F27.wireOp",EDGE,"E55")])]}),makeQuery(id+"F32.opExtrude","SWEPT_FACE",FACE,{"disambiguationData":[OSD([sQuery(id+"F31.wireOp",EDGE,"E74")])]})]});
            fillet(context, id + "F36", {"entities" : qUnion([Q0, Q1, Q2, Q3]), "radius" : 0.25 * mm, "tangentPropagation" : true, "allowEdgeOverflow" : false});
        }
        {
            var Q0;
            {var subQ0=sQuery(id+"F27.wireOp",EDGE,"E57");Q0=makeQuery(id+"F30.boolean.opBoolean","SPLIT",EDGE,{"disambiguationData":[TD([makeQuery(id+"F30.opExtrude","SWEPT_FACE",FACE,{"disambiguationData":[OSD([sQuery(id+"F29.wireOp",EDGE,"E63")])]})])],"derivedFrom":makeQuery(id+"F28.opExtrude","CAP_EDGE",EDGE,{"disambiguationData":[OSD([subQ0])],"isStart":false})});}
            var Q1;
            {var subQ0=sQuery(id+"F27.wireOp",EDGE,"E55");var subQ1=sQuery(id+"F27.wireOp",EDGE,"E57");Q1=makeQuery(id+"F30.boolean.opBoolean","SPLIT",EDGE,{"disambiguationData":[TD([makeQuery(id+"F28.opExtrude","SWEPT_FACE",FACE,{"disambiguationData":[OSD([subQ0])]})])],"derivedFrom":makeQuery(id+"F28.opExtrude","CAP_EDGE",EDGE,{"disambiguationData":[OSD([subQ1])],"isStart":false})});}
            fillet(context, id + "F37", {"entities" : qUnion([Q0, Q1]), "radius" : 2.54 * mm, "tangentPropagation" : true, "allowEdgeOverflow" : false});
        }
    });
